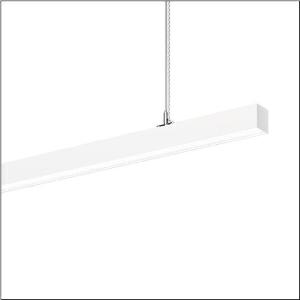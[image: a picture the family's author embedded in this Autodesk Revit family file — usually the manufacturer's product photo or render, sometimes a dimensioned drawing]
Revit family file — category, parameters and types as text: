
# Revit family: silica_r__21_51mx33da37wb_a2a9
name_source: partatom
category: Lighting Fixtures
units: mm (PartAtom-declared; Revit-internal decimal feet)

## family parameters
Cut with Voids When Loaded = No
Host = Face
Light Source = No
Part Type = Normal
Room Calculation Point = No
Round Connector Dimension = Use Diameter
Shared = No

## types (1)
- --- (1 x LED, 5910 lm, 41.3 W, 3000K)
    Apparent Load = 41 VA
    CIE Flux Codes = 78 96 99 55 100
    Color Rendering = 80
    Color Temperature = 3000K
    Default Elevation = 1800 mm
    Description = Silica® 21, office luminaire, primary optical cover: prismatic diffuser, of PMMA, CAT 2 (L<= 3000cd/m²), light emission: direct/indirect distribution, primary light characteristic: symmetric, installation type: suspended mounting, LED, rated luminous flux: 5.910lm, luminous efficacy: 143lm/W, light colour: 830, colour temperature: 3000K, with terminal, 3+2-pole, max. 2.5mm², mains connection: 220..240V, AC, 50/60Hz, rated input power: 41.3W, luminaire housing, of aluminium, traffic white (RAL 9016), length: 1.204mm, width: 53mm, height: 53mm, protection rating (complete): IP20, insulation class (complete): insulation class I (protective earthing), certification: CE, permissible operating ambient temperature: 0..+35°C, standard: EN 50419, packaging unit: 1 piece
    Height = 53 mm
    Lamp = 1 x LED
    Lamp Light Flux = 5910 lm
    Lamp Power = 41.3 W
    Lamp count = 1
    Length = 1204 mm
    Luminous efficacy = 143 lm/W
    Manufacturer = Siteco
    ModVariant = No
    Model = 51MX33DA37WB
    Mounting Place = Ceiling
    Mounting Type = Pendant
    Number of Poles = 1
    OnlyDefault = Yes
    Power Factor = 1
    Product Name = Silica® 21
    Product group = office luminaire | ceiling pendant
    ProductGroupID = 902
    Protection Class = Protection class I
    Protection Degree = IP 20
    RLX_Detail_Level = 1
    RLX_Emergency_Light_Flux = 0 lm
    RLX_Emergency_Type = 0
    RLX_Emergency_Type_DB = No
    RlxData = <blob elided: 21409 chars, md5=a6b7057a>
    Socket = socket
    Standby Power = 0 W
    System Light Flux = 5910 lm
    System Power = 41 W
    Type Comments = factory setting: luminous flux: 100 % | dim-lin: 254 | 345 mA
    Type Image = l_1297784.jpg
    URL = http://relux.com
    VarID = @adj_049237
    Voltage = 0 V
    Weight = 0.00 kg
    Width = 53 mm

## geometry (parser evidence)
native form markers: Blend x4, Sweep x15
no freeform markers — native parametric forms only
